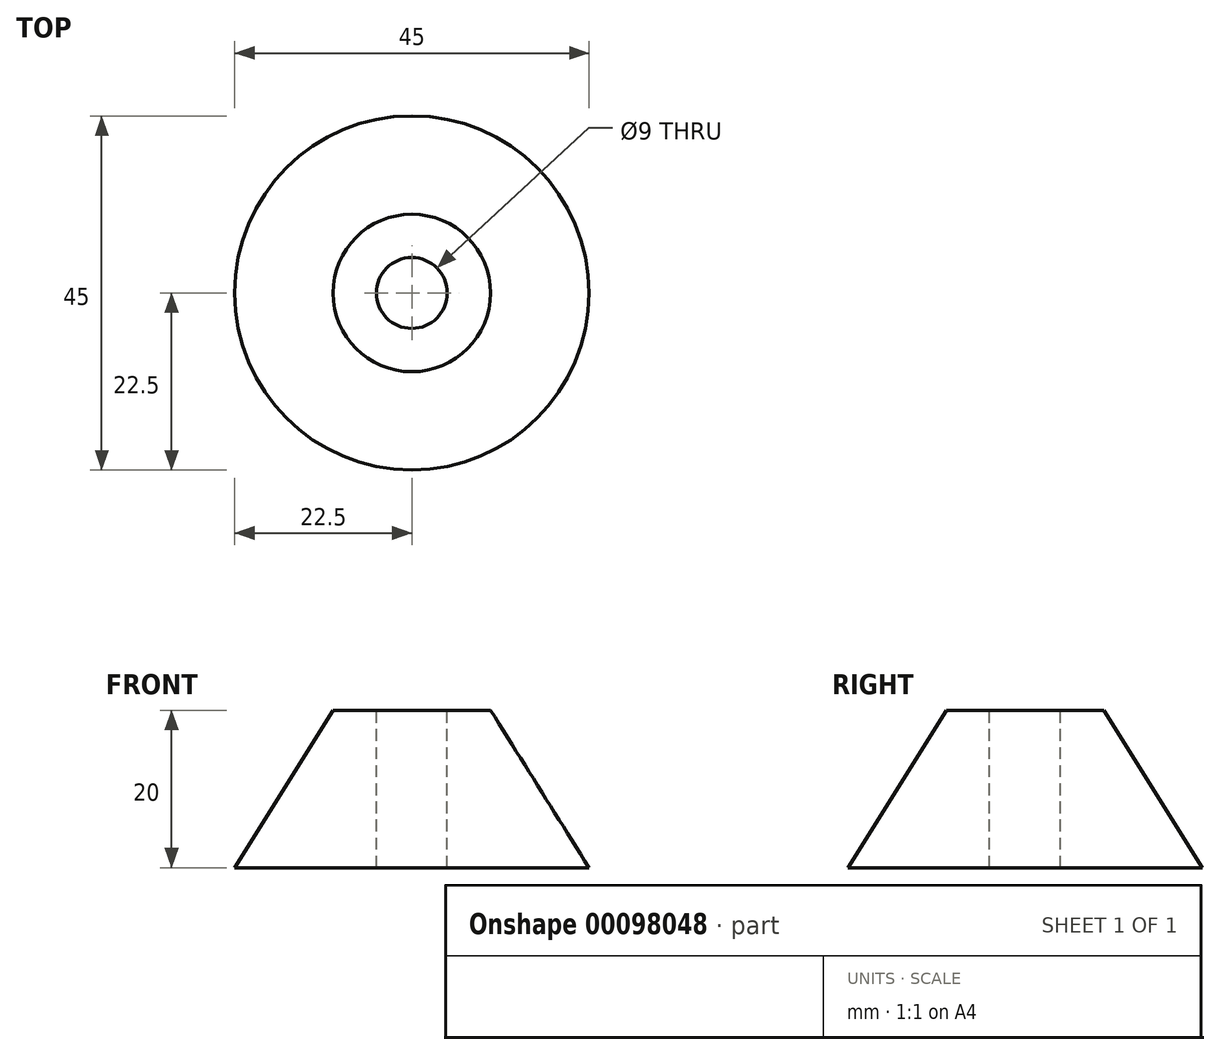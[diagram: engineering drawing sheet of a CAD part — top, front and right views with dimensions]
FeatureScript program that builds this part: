
annotation { "Feature Type Name" : "Feature", "Feature Type Description" : "" }
export const myFeature = defineFeature(function(context is Context, id is Id, definition is map)
    precondition{}
    {
        {
            var Q0;
            Q0=qCreatedBy(makeId("Top.planeOp"),FACE);
            var sketch = newSketch(context, id + "F0", { "sketchPlane" : qUnion([Q0])});
            skCircle(sketch, "E0", {"center": v(0, 0) * mm, "radius": 22.5 * mm});
            skSolve(sketch);
        }
        {
            var Q0;
            Q0=qCreatedBy(makeId("Top.planeOp"),FACE);
            cPlane(context, id + "F1", {"entities" : qUnion([Q0]), "cplaneType" : CPlaneType.OFFSET, "offset" : 20 * mm, "width" : 150 * mm, "height" : 150 * mm});
        }
        {
            var Q0;
            Q0=qCreatedBy(id+"F1.planeOp",FACE);
            var sketch = newSketch(context, id + "F2", { "sketchPlane" : qUnion([Q0])});
            skCircle(sketch, "E1", {"center": v(0, 0) * mm, "radius": 10 * mm});
            skSolve(sketch);
        }
        {
            var Q0;
            Q0=makeQuery(id+"F0.imprint","IMPRINT",FACE,{"disambiguationData":[TD([[makeQuery(id+"F0.imprint","IMPRINT",EDGE,{"derivedFrom":sQuery(id+"F0.wireOp",EDGE,"E0")}),1.0]])]});
            var Q1;
            Q1=makeQuery(id+"F2.imprint","IMPRINT",FACE,{"disambiguationData":[TD([[makeQuery(id+"F2.imprint","IMPRINT",EDGE,{"derivedFrom":sQuery(id+"F2.wireOp",EDGE,"E1")}),1.0]])]});
            loft(context, id + "F3", {"sheetProfilesArray" : [{ "sheetProfileEntities" : qUnion([Q0]) }, { "sheetProfileEntities" : qUnion([Q1]) }]});
        }
        {
            var Q0;
            Q0=makeQuery(id+"F3.opLoft","CAP_FACE",FACE,{"disambiguationData":[OSD([makeQuery(id+"F2.imprint","IMPRINT",FACE,{"disambiguationData":[TD([[makeQuery(id+"F2.imprint","IMPRINT",EDGE,{"derivedFrom":sQuery(id+"F2.wireOp",EDGE,"E1")}),1.0]])]})])],"isStart":true});
            var sketch = newSketch(context, id + "F4", { "sketchPlane" : qUnion([Q0])});
            skCircle(sketch, "E2", {"center": v(0, 0) * mm, "radius": 4.5 * mm});
            skSolve(sketch);
        }
        {
            var Q0;
            Q0 = qSketchRegion(id + "F4", true);
            extrude(context, id + "F5", {"entities" : qUnion([Q0]), "operationType" : NewBodyOperationType.REMOVE, "endBound" : BoundingType.THROUGH_ALL, "oppositeDirection" : true, "depth" : 25 * mm});
        }
    });
